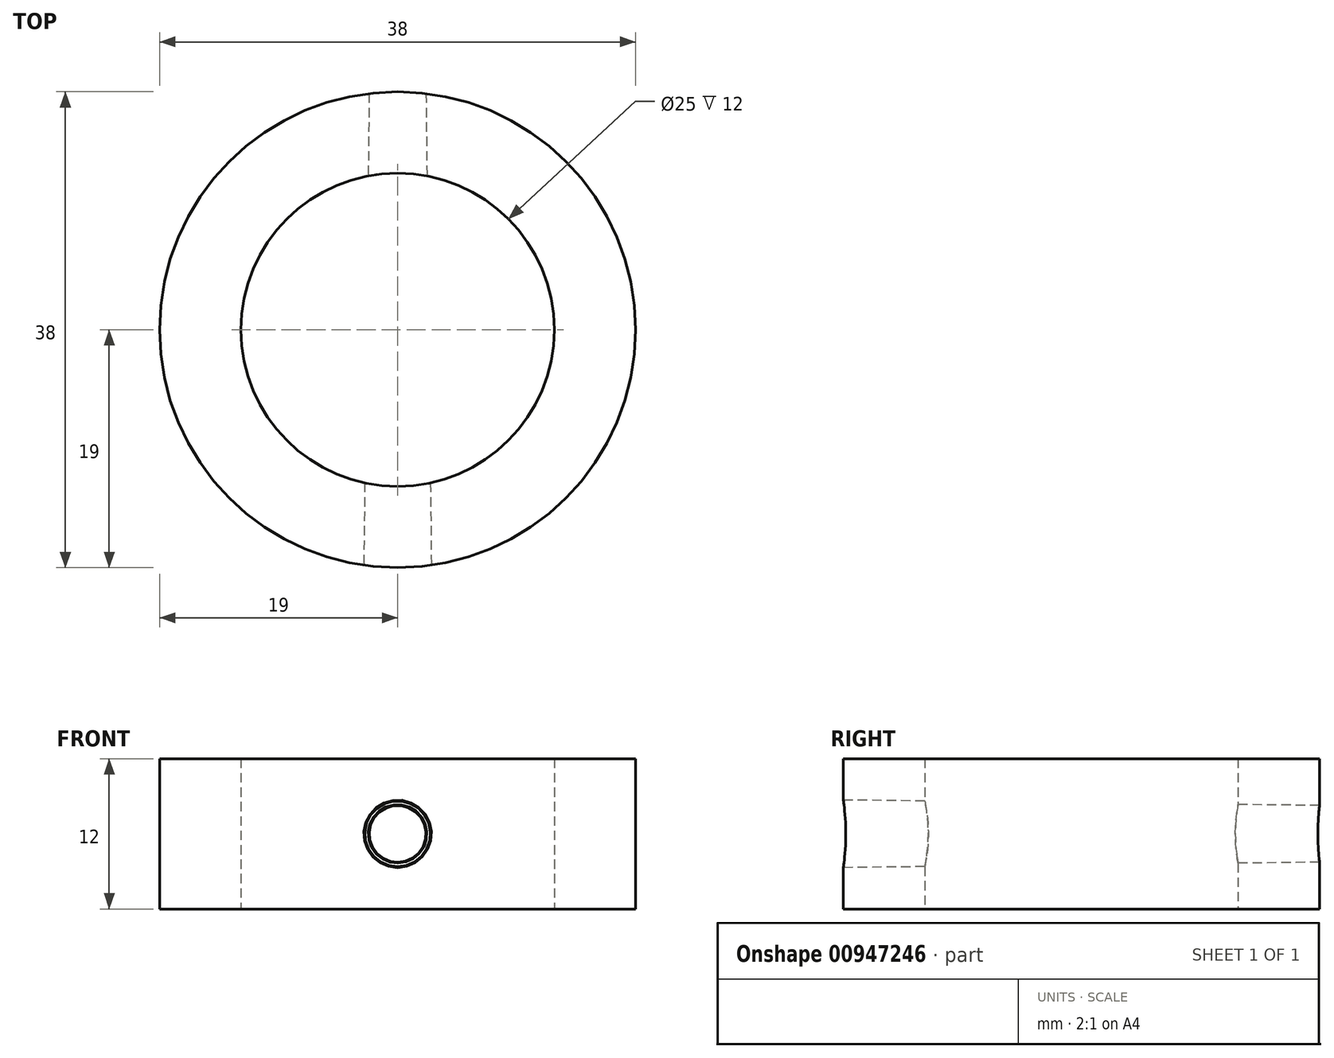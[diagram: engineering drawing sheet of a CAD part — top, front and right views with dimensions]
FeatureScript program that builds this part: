
annotation { "Feature Type Name" : "Feature", "Feature Type Description" : "" }
export const myFeature = defineFeature(function(context is Context, id is Id, definition is map)
    precondition{}
    {
        {
            var Q0;
            Q0=qCreatedBy(makeId("Top.planeOp"),FACE);
            var sketch = newSketch(context, id + "F0", { "sketchPlane" : qUnion([Q0])});
            skCircle(sketch, "E0", {"center": v(0, 0) * mm, "radius": 19 * mm});
            skCircle(sketch, "E1", {"center": v(0, 0) * mm, "radius": 12.5 * mm});
            skSolve(sketch);
        }
        {
            var Q0;
            Q0 = qSketchRegion(id + "F0", true);
            extrude(context, id + "F1", {"entities" : qUnion([Q0]), "depth" : 12 * mm, "offsetDistance" : 25 * mm});
        }
        {
            var Q0;
            Q0=qCreatedBy(makeId("Front.planeOp"),FACE);
            cPlane(context, id + "F2", {"entities" : qUnion([Q0]), "cplaneType" : CPlaneType.OFFSET, "offset" : 29 * mm, "width" : 150 * mm, "height" : 150 * mm});
        }
        {
            var Q0;
            Q0=qCreatedBy(id+"F2.planeOp",FACE);
            var sketch = newSketch(context, id + "F3", { "sketchPlane" : qUnion([Q0])});
            skCircle(sketch, "E2", {"center": v(0, 6) * mm, "radius": 2.81 * mm});
            skSolve(sketch);
        }
        {
            var Q0;
            Q0=qCreatedBy(makeId("Front.planeOp"),FACE);
            cPlane(context, id + "F4", {"entities" : qUnion([Q0]), "cplaneType" : CPlaneType.OFFSET, "offset" : 29 * mm, "oppositeDirection" : true, "width" : 150 * mm, "height" : 150 * mm});
        }
        {
            var Q0;
            Q0=qCreatedBy(id+"F4.planeOp",FACE);
            var sketch = newSketch(context, id + "F5", { "sketchPlane" : qUnion([Q0])});
            skCircle(sketch, "E3", {"center": v(0, 6) * mm, "radius": 2.15 * mm});
            skSolve(sketch);
        }
        {
            var Q1;
            Q1=makeQuery(id+"F3.imprint","IMPRINT",FACE,{"disambiguationData":[TD([[makeQuery(id+"F3.imprint","IMPRINT",EDGE,{"derivedFrom":sQuery(id+"F3.wireOp",EDGE,"E2")}),1.0]])]});
            var Q2;
            Q2=makeQuery(id+"F5.imprint","IMPRINT",FACE,{"disambiguationData":[TD([[makeQuery(id+"F5.imprint","IMPRINT",EDGE,{"derivedFrom":sQuery(id+"F5.wireOp",EDGE,"E3")}),1.0]])]});
            loft(context, id + "F6", {"operationType" : NewBodyOperationType.REMOVE, "sheetProfilesArray" : [{ "sheetProfileEntities" : qUnion([Q1]) }, { "sheetProfileEntities" : qUnion([Q2]) }]});
        }
    });
